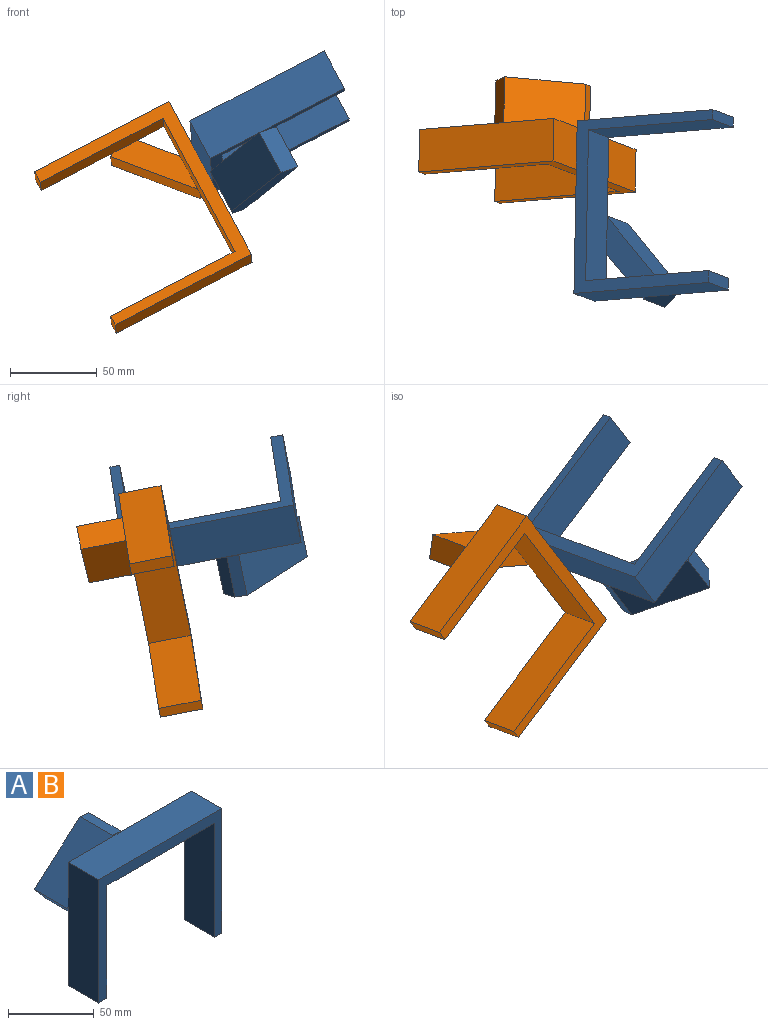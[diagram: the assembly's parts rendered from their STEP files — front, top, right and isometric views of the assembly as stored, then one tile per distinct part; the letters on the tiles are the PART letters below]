
ASSEMBLY  parts=2 mates=1
PART A: 21 faces, bbox 102.8x51.7x89.5 mm
  f0: plane 35.78x31.1mm, normal (0,1,0), area 380.6mm2, adj f2,f3,f7,f8,f18
  f1: plane 88.75x57.66mm, normal (0,1,0), area 883.4mm2, adj f3,f4,f5,f6,f7,f17,f19
  f2: plane 80.22x25mm, normal (1,0,0), area 2005.6mm2, adj f0,f3,f9,f10,f11,f12
  f3: plane 88.77x25mm, normal (0,0,-1), area 2219.3mm2, adj f0,f1,f2,f4,f10,f12
  f4: plane 81.23x25mm, normal (-1,0,0), area 2030.8mm2, adj f1,f3,f5,f10
  f5: plane 25x5.83mm, normal (0,0,-1), area 145.8mm2, adj f1,f4,f6,f10
  f6: plane 88.75x25mm, normal (1,0,0), area 2218.8mm2, adj f1,f5,f7,f10
  f7: plane 101.63x25mm, normal (0,0,1), area 2540.7mm2, adj f0,f1,f6,f8,f10,f13
  f8: plane 87.74x25mm, normal (-1,0,0), area 2193.6mm2, adj f0,f7,f9,f10,f11,f16
  f9: plane 25x7.02mm, normal (0,0,-1), area 175.6mm2, adj f2,f8,f10,f11
  f10: plane 101.63x88.75mm, normal (0,-1,0), area 1801.4mm2, adj f2,f3,f4,f5,f6,f7,f8,f9
  f11: plane 54.29x7.02mm, normal (0,1,0), area 352.9mm2, adj f2,f8,f9,f15
  f12: plane 42.05x35.46mm, normal (0,-1,0), area 591.2mm2, adj f2,f3,f15,f18,f19
  f13: plane 8.19x0.77mm, normal (0,-1,0), area 4.1mm2, adj f7,f17,f18,f20
  f14: plane 51.05x43.75mm, normal (0,1,0), area 781.2mm2, adj f15,f17,f18,f19,f20
  f15: plane 26.74x10.87mm, normal (-0.75,0,-0.66), area 385mm2, adj f11,f12,f14,f16,f18,f19
  f16: plane 2.35x1.16mm, normal (0,-1,0), area 1.4mm2, adj f8,f15,f18
  f17: plane 26.74x7.09mm, normal (0.75,0,0.66), area 251.3mm2, adj f1,f13,f14,f19,f20
  f18: plane 37.83x32.89mm, normal (-0.66,0,0.75), area 1340.2mm2, adj f0,f12,f13,f14,f15,f16,f20
  f19: plane 41.6x36.17mm, normal (0.66,0,-0.75), area 1473.9mm2, adj f1,f12,f14,f15,f17
  f20: plane 26.74x7.05mm, normal (0.07,0,1), area 189.1mm2, adj f13,f14,f17,f18
PART B: same geometry as A
PLACE A rot(axis=(-0.68,-0.59,0.44),144deg) t=(66.71,-339.65,123.8)mm
PLACE B rot(axis=(-0.15,0.98,-0.11),62.9deg) t=(-10.18,-298.07,78.4)mm
MATE planar B.f7 <-> A.f7  axis (0.88,0.07,0.46) through (28,-307.41,99.83)mm
